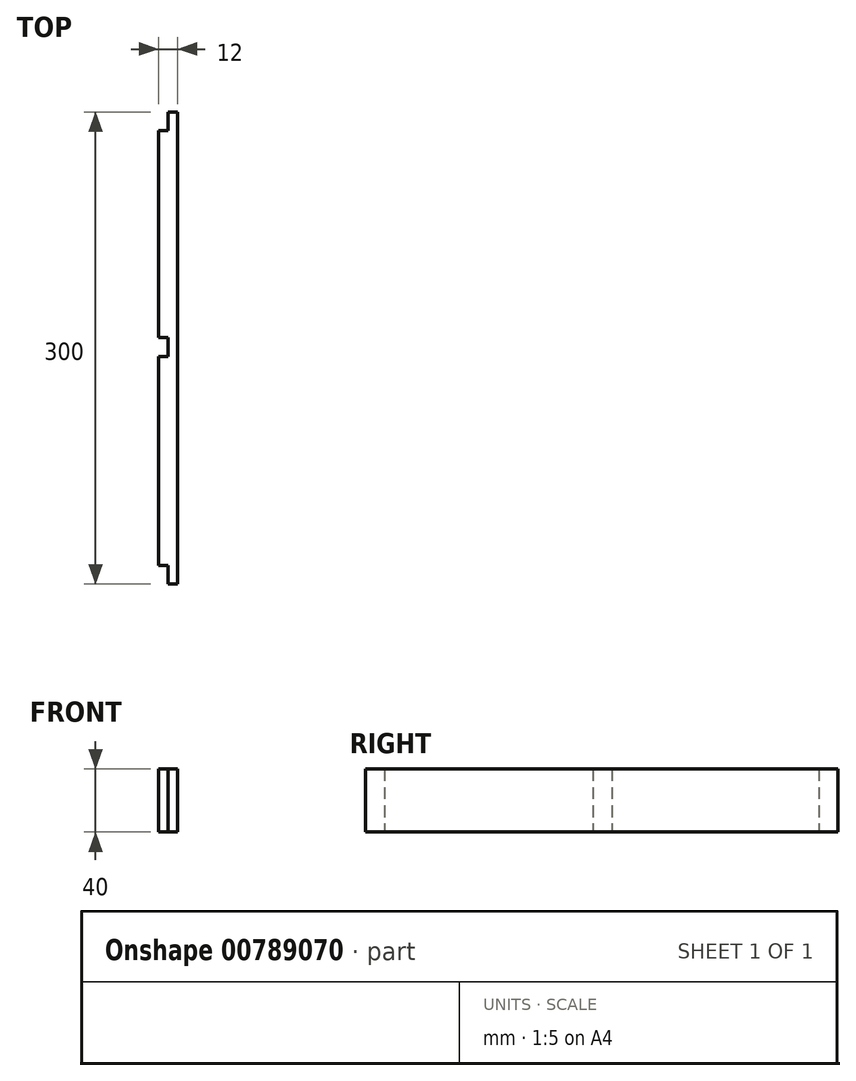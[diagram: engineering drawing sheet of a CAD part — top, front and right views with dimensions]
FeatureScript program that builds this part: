
annotation { "Feature Type Name" : "Feature", "Feature Type Description" : "" }
export const myFeature = defineFeature(function(context is Context, id is Id, definition is map)
    precondition{}
    {
        {
            var Q0;
            Q0=qCreatedBy(makeId("Top.planeOp"),FACE);
            var sketch = newSketch(context, id + "F0", { "sketchPlane" : qUnion([Q0])});
            skLineSegment(sketch, "E0.bottom", {"start": v(0, 0) * mm, "end": v(-6, 0) * mm});
            skLineSegment(sketch, "E0.top", {"start": v(0, 300) * mm, "end": v(-6, 300) * mm});
            skLineSegment(sketch, "E0.left", {"start": v(0, 0) * mm, "end": v(0, 300) * mm});
            skLineSegment(sketch, "E0.right", {"start": v(-12, 12) * mm, "end": v(-12, 144.66) * mm});
            skLineSegment(sketch, "E1", {"start": v(-6, 0) * mm, "end": v(-6, 12) * mm});
            skLineSegment(sketch, "E2", {"start": v(-6, 12) * mm, "end": v(-12, 12) * mm});
            skPoint(sketch, "E3.orphan", {"position": v(-12, 0) * mm});
            skLineSegment(sketch, "E4", {"start": v(-6, 300) * mm, "end": v(-6, 288) * mm});
            skLineSegment(sketch, "E5", {"start": v(-6, 288) * mm, "end": v(-12, 288) * mm});
            skPoint(sketch, "E6.orphan", {"position": v(-12, 300) * mm});
            skLineSegment(sketch, "E7", {"start": v(-6.08, 150.3) * mm, "end": v(-6.08, 144.66) * mm});
            skLineSegment(sketch, "E8", {"start": v(-6.08, 144.66) * mm, "end": v(-12, 144.66) * mm});
            skLineSegment(sketch, "E9", {"start": v(-6.08, 150.3) * mm, "end": v(-6.08, 156.66) * mm});
            skLineSegment(sketch, "E10", {"start": v(-6.08, 156.66) * mm, "end": v(-12, 156.66) * mm});
            skLineSegment(sketch, "E11.trimOffspring", {"start": v(-12, 156.66) * mm, "end": v(-12, 288) * mm});
            skSolve(sketch);
        }
        {
            var Q0;
            Q0=makeQuery(id+"F0.imprint","IMPRINT",FACE,{"disambiguationData":[TD([[makeQuery(id+"F0.imprint","IMPRINT",EDGE,{"derivedFrom":sQuery(id+"F0.wireOp",EDGE,"E0.bottom")}),-1.0]])]});
            extrude(context, id + "F1", {"entities" : qUnion([Q0]), "depth" : 40 * mm, "offsetDistance" : 25 * mm});
        }
    });
